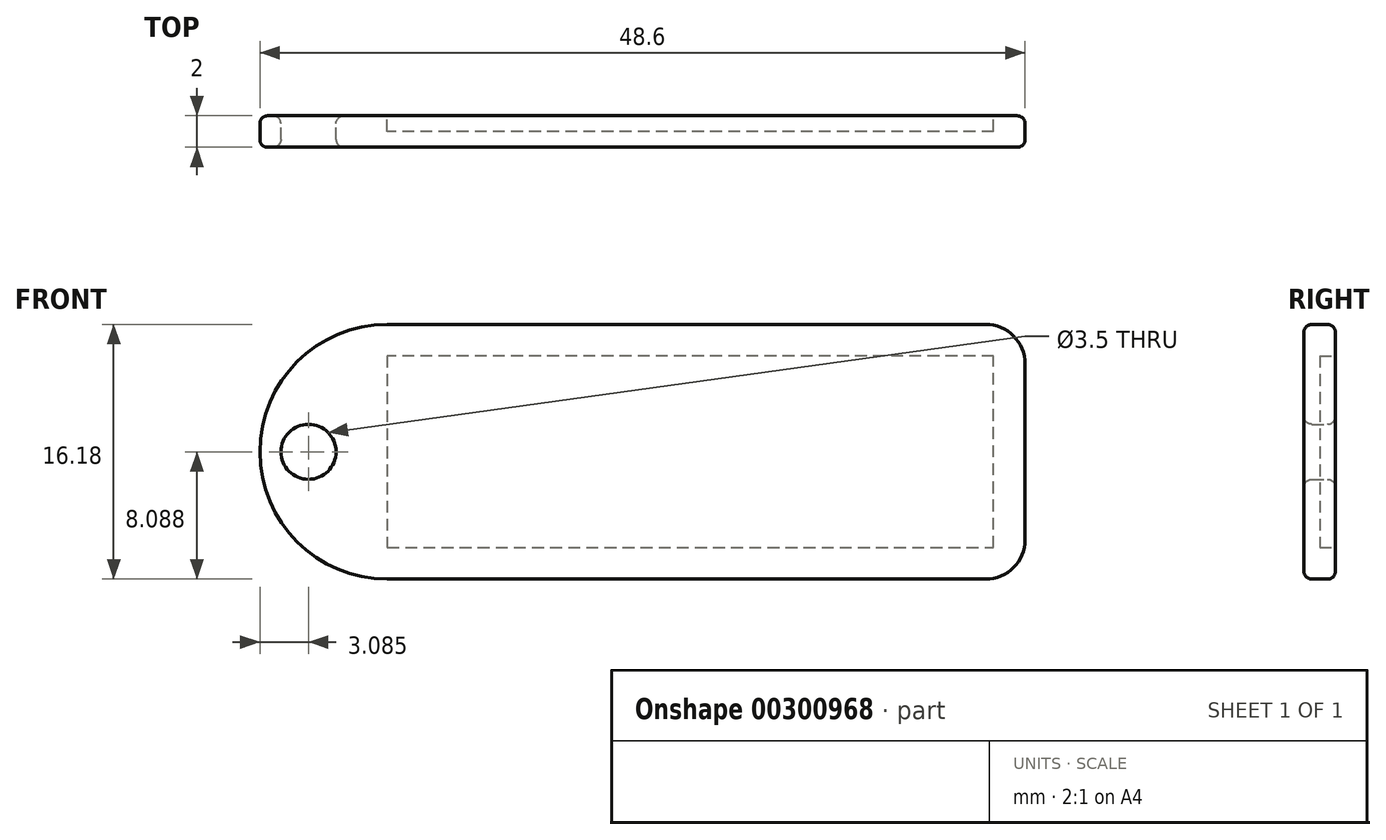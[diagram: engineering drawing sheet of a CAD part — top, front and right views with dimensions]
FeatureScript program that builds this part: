
annotation { "Feature Type Name" : "Feature", "Feature Type Description" : "" }
export const myFeature = defineFeature(function(context is Context, id is Id, definition is map)
    precondition{}
    {
        {
            var Q0;
            Q0=qCreatedBy(makeId("Front.planeOp"),FACE);
            var sketch = newSketch(context, id + "F0", { "sketchPlane" : qUnion([Q0])});
            skLineSegment(sketch, "E0.bottom", {"start": v(-2.5, 0) * mm, "end": v(-40.52, 0) * mm});
            skLineSegment(sketch, "E0.top", {"start": v(-2.5, 16.18) * mm, "end": v(-40.52, 16.18) * mm});
            skLineSegment(sketch, "E0.left", {"start": v(0, 2.5) * mm, "end": v(0, 13.68) * mm});
            skArc(sketch, "E1", {"start": v(-40.52, 16.18) * mm, "mid": v(-48.6, 8.09) * mm, "end": v(-40.52, 0) * mm});
            skPoint(sketch, "E2.visualSharp", {"position": v(0, 16.18) * mm});
            skArc(sketch, "E2.filletArc", {"start": v(0, 13.68) * mm, "mid": v(-0.73, 15.44) * mm, "end": v(-2.5, 16.18) * mm});
            skPoint(sketch, "E3.visualSharp", {"position": v(0, 0) * mm});
            skArc(sketch, "E3.filletArc", {"start": v(-2.5, 0) * mm, "mid": v(-0.73, 0.73) * mm, "end": v(0, 2.5) * mm});
            skCircle(sketch, "E4", {"center": v(-45.52, 8.09) * mm, "radius": 1.75 * mm});
            skSolve(sketch);
        }
        {
            var Q0;
            Q0=qCreatedBy(makeId("Front.planeOp"),FACE);
            var sketch = newSketch(context, id + "F1", { "sketchPlane" : qUnion([Q0])});
            skLineSegment(sketch, "E5.0", {"start": v(-2, 2) * mm, "end": v(-2, 14.18) * mm});
            skLineSegment(sketch, "E5.1", {"start": v(-40.52, 2) * mm, "end": v(-2, 2) * mm});
            skArc(sketch, "E5.2", {"start": v(-40.52, 14.18) * mm, "mid": v(-46.6, 8.09) * mm, "end": v(-40.52, 2) * mm});
            skLineSegment(sketch, "E5.3", {"start": v(-2, 14.18) * mm, "end": v(-40.52, 14.18) * mm});
            skSolve(sketch);
        }
        {
            var Q0;
            Q0=makeQuery(id+"F0.imprint","IMPRINT",FACE,{"disambiguationData":[TD([[makeQuery(id+"F0.imprint","IMPRINT",EDGE,{"derivedFrom":sQuery(id+"F0.wireOp",EDGE,"E0.bottom")}),-1.0]])]});
            extrude(context, id + "F2", {"entities" : qUnion([Q0]), "depth" : 2 * mm});
        }
        {
            var Q0;
            Q0=makeQuery(id+"F1.imprint","IMPRINT",FACE,{"disambiguationData":[TD([[makeQuery(id+"F1.imprint","IMPRINT",EDGE,{"derivedFrom":sQuery(id+"F1.wireOp",EDGE,"E5.0")}),1.0]])]});
            extrude(context, id + "F3", {"entities" : qUnion([Q0]), "operationType" : NewBodyOperationType.REMOVE, "depth" : 1 * mm});
        }
        {
            var Q0;
            Q0=makeQuery(id+"F3.boolean.opBoolean","COPY",FACE,{"derivedFrom":makeQuery(id+"F3.opExtrude","CAP_FACE",FACE,{"disambiguationData":[OSD([sQuery(id+"F1.wireOp",EDGE,"E5.0"),sQuery(id+"F1.wireOp",EDGE,"E5.1"),sQuery(id+"F1.wireOp",EDGE,"E5.2"),sQuery(id+"F1.wireOp",EDGE,"E5.3")])],"isStart":false})});
            var sketch = newSketch(context, id + "F4", { "sketchPlane" : qUnion([Q0])});
            skLineSegment(sketch, "E6", {"start": v(40.52, 14.18) * mm, "end": v(40.52, 2) * mm});
            skSolve(sketch);
        }
        {
            var Q0;
            Q0=makeQuery(id+"F4.imprint","IMPRINT",FACE,{"disambiguationData":[TD([[makeQuery(id+"F4.imprint","IMPRINT",EDGE,{"derivedFrom":sQuery(id+"F4.wireOp",EDGE,"E6")}),1.0]])]});
            extrude(context, id + "F5", {"entities" : qUnion([Q0]), "operationType" : NewBodyOperationType.ADD, "depth" : 1 * mm});
        }
        {
            var Q0;
            Q0=makeQuery(id+"F3.boolean.opBoolean","COPY",FACE,{"derivedFrom":makeQuery(id+"F3.opExtrude","CAP_FACE",FACE,{"disambiguationData":[OSD([sQuery(id+"F1.wireOp",EDGE,"E5.0"),sQuery(id+"F1.wireOp",EDGE,"E5.1"),sQuery(id+"F1.wireOp",EDGE,"E5.2"),sQuery(id+"F1.wireOp",EDGE,"E5.3")])],"isStart":false})});
            var sketch = newSketch(context, id + "F6", { "sketchPlane" : qUnion([Q0])});
            skText(sketch, "E7", { "text": "Lenda", "fontName": "OpenSans-Bold.ttf"});
            const initialGuessF6  = {"E7": [0.00615, 0.0048, 1, 0, 0.0048]};
            skSetInitialGuess(sketch, initialGuessF6);
            skSolve(sketch);
        }
        {
            var Q0;
            Q0 = qConstructionFilter(qBodyType(qCreatedBy(id + "F6" ,EDGE), BodyType.WIRE), ConstructionObject.NO);
            extrude(context, id + "F7", {"bodyType" : ToolBodyType.SURFACE, "surfaceEntities" : qUnion([Q0]), "depth" : 1 * mm});
        }
        {
            var Q0;
            Q0=makeQuery(id+"F2.opExtrude","CAP_EDGE",EDGE,{"disambiguationData":[OSD([sQuery(id+"F0.wireOp",EDGE,"E1")])],"isStart":true});
            var Q1;
            Q1=makeQuery(id+"F2.opExtrude","CAP_EDGE",EDGE,{"disambiguationData":[OSD([sQuery(id+"F0.wireOp",EDGE,"E1")])],"isStart":false});
            var Q2;
            {var subQ0=sQuery(id+"F0.wireOp",EDGE,"E4");Q2=makeQuery(id+"F5.boolean.opBoolean","MERGE",EDGE,{"derivedFrom":[makeQuery(id+"F2.opExtrude","CAP_EDGE",EDGE,{"disambiguationData":[OSD([subQ0])],"isStart":true}),makeQuery(id+"F5.opExtrude","CAP_EDGE",EDGE,{"disambiguationData":[OSD([subQ0,sQuery(id+"F1.wireOp",EDGE,"E5.0"),sQuery(id+"F1.wireOp",EDGE,"E5.1"),sQuery(id+"F1.wireOp",EDGE,"E5.2"),sQuery(id+"F1.wireOp",EDGE,"E5.3")])],"isStart":false})]});}
            var Q3;
            Q3=makeQuery(id+"F2.opExtrude","CAP_EDGE",EDGE,{"disambiguationData":[OSD([sQuery(id+"F0.wireOp",EDGE,"E4")])],"isStart":false});
            fillet(context, id + "F8", {"entities" : qUnion([Q0, Q1, Q2, Q3]), "radius" : 0.5 * mm, "tangentPropagation" : true, "allowEdgeOverflow" : false});
        }
    });
